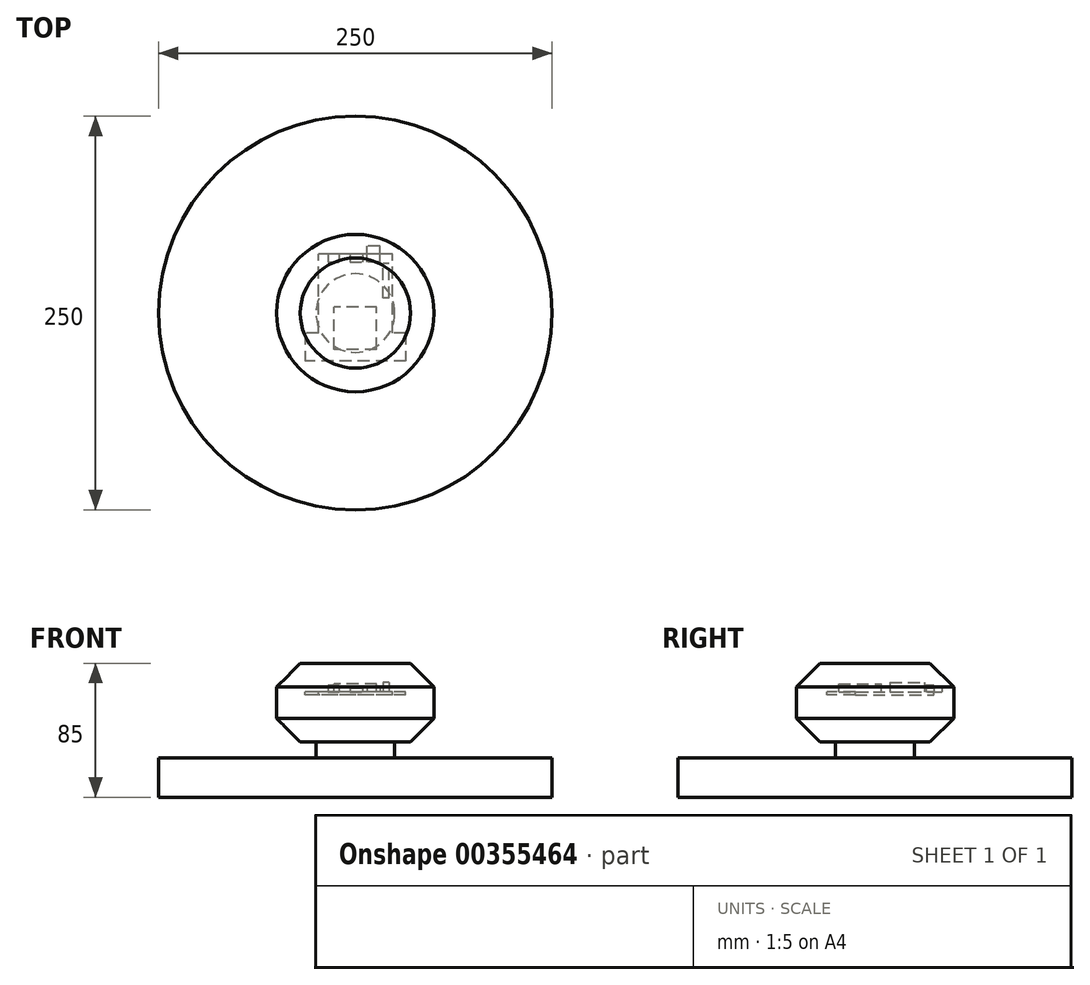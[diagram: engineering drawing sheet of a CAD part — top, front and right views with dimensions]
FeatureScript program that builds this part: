
annotation { "Feature Type Name" : "Feature", "Feature Type Description" : "" }
export const myFeature = defineFeature(function(context is Context, id is Id, definition is map)
    precondition{}
    {
        {
            var Q0;
            Q0=qCreatedBy(makeId("Top.planeOp"),FACE);
            var sketch = newSketch(context, id + "F0", { "sketchPlane" : qUnion([Q0])});
            skLineSegment(sketch, "E0.bottom", {"start": v(13.5, -13.5) * mm, "end": v(-13.5, -13.5) * mm});
            skLineSegment(sketch, "E0.top", {"start": v(13.5, 13.5) * mm, "end": v(-13.5, 13.5) * mm});
            skLineSegment(sketch, "E0.left", {"start": v(13.5, -13.5) * mm, "end": v(13.5, 13.5) * mm});
            skLineSegment(sketch, "E0.right", {"start": v(-13.5, -13.5) * mm, "end": v(-13.5, 13.5) * mm});
            skPoint(sketch, "E0.middle", {"position": v(0, 0) * mm});
            skSolve(sketch);
        }
        {
            var Q0;
            Q0=makeQuery(id+"F0.imprint","IMPRINT",FACE,{"disambiguationData":[TD([[makeQuery(id+"F0.imprint","IMPRINT",EDGE,{"derivedFrom":sQuery(id+"F0.wireOp",EDGE,"E0.bottom")}),-1.0]])]});
            extrude(context, id + "F1", {"entities" : qUnion([Q0]), "oppositeDirection" : true, "depth" : 2 * mm});
        }
        {
            var Q0;
            Q0=makeQuery(id+"F1.opExtrude","CAP_FACE",FACE,{"disambiguationData":[OSD([sQuery(id+"F0.wireOp",EDGE,"E0.bottom"),sQuery(id+"F0.wireOp",EDGE,"E0.top"),sQuery(id+"F0.wireOp",EDGE,"E0.left"),sQuery(id+"F0.wireOp",EDGE,"E0.right")])],"isStart":false});
            cPlane(context, id + "F2", {"entities" : qUnion([Q0]), "cplaneType" : CPlaneType.OFFSET, "offset" : 3 * mm, "width" : 150 * mm, "height" : 150 * mm});
        }
        {
            var Q0;
            Q0=qCreatedBy(id+"F2.planeOp",FACE);
            var sketch = newSketch(context, id + "F3", { "sketchPlane" : qUnion([Q0])});
            skLineSegment(sketch, "E1", {"start": v(0, 0) * mm, "end": v(0, -22) * mm, "construction": true});
            skLineSegment(sketch, "E2.bottom", {"start": v(23.5, 3) * mm, "end": v(-23.5, 3) * mm});
            skLineSegment(sketch, "E2.top", {"start": v(23.5, -47) * mm, "end": v(-23.5, -47) * mm});
            skLineSegment(sketch, "E2.left", {"start": v(23.5, 3) * mm, "end": v(23.5, -47) * mm});
            skLineSegment(sketch, "E2.right", {"start": v(-23.5, 3) * mm, "end": v(-23.5, -47) * mm});
            skPoint(sketch, "E2.middle", {"position": v(0, -22) * mm});
            skSolve(sketch);
        }
        {
            var Q0;
            Q0=makeQuery(id+"F3.imprint","IMPRINT",FACE,{"disambiguationData":[TD([[makeQuery(id+"F3.imprint","IMPRINT",EDGE,{"derivedFrom":sQuery(id+"F3.wireOp",EDGE,"E2.bottom")}),1.0]])]});
            extrude(context, id + "F4", {"entities" : qUnion([Q0]), "depth" : 2 * mm});
        }
        {
            var Q0;
            Q0=makeQuery(id+"F4.opExtrude","CAP_FACE",FACE,{"disambiguationData":[OSD([sQuery(id+"F3.wireOp",EDGE,"E2.bottom"),sQuery(id+"F3.wireOp",EDGE,"E2.top"),sQuery(id+"F3.wireOp",EDGE,"E2.left"),sQuery(id+"F3.wireOp",EDGE,"E2.right")])],"isStart":true});
            var sketch = newSketch(context, id + "F5", { "sketchPlane" : qUnion([Q0])});
            skLineSegment(sketch, "E3", {"start": v(0, -3) * mm, "end": v(0, -12) * mm, "construction": true});
            skPoint(sketch, "E3.endSnap0", {"position": v(0, -3) * mm});
            skLineSegment(sketch, "E4.bottom", {"start": v(32, -3) * mm, "end": v(-32, -3) * mm});
            skLineSegment(sketch, "E4.top", {"start": v(32, -21) * mm, "end": v(-32, -21) * mm});
            skLineSegment(sketch, "E4.left", {"start": v(32, -3) * mm, "end": v(32, -21) * mm});
            skLineSegment(sketch, "E4.right", {"start": v(-32, -3) * mm, "end": v(-32, -21) * mm});
            skPoint(sketch, "E4.middle", {"position": v(0, -12) * mm});
            skSolve(sketch);
        }
        {
            var Q0;
            Q0=makeQuery(id+"F5.imprint","IMPRINT",FACE,{"disambiguationData":[TD([[makeQuery(id+"F5.imprint","IMPRINT",EDGE,{"derivedFrom":sQuery(id+"F5.wireOp",EDGE,"E4.top")}),-1.0]])]});
            extrude(context, id + "F6", {"entities" : qUnion([Q0]), "operationType" : NewBodyOperationType.ADD, "oppositeDirection" : true, "depth" : 2 * mm});
        }
        {
            var Q0;
            Q0=makeQuery(id+"F1.opExtrude","CAP_FACE",FACE,{"disambiguationData":[OSD([sQuery(id+"F0.wireOp",EDGE,"E0.bottom"),sQuery(id+"F0.wireOp",EDGE,"E0.top"),sQuery(id+"F0.wireOp",EDGE,"E0.left"),sQuery(id+"F0.wireOp",EDGE,"E0.right")])],"isStart":false});
            var Q1;
            Q1=makeQuery(id+"F6.boolean.opBoolean","MERGE",FACE,{"derivedFrom":[makeQuery(id+"F4.opExtrude","CAP_FACE",FACE,{"disambiguationData":[OSD([sQuery(id+"F3.wireOp",EDGE,"E2.bottom"),sQuery(id+"F3.wireOp",EDGE,"E2.top"),sQuery(id+"F3.wireOp",EDGE,"E2.left"),sQuery(id+"F3.wireOp",EDGE,"E2.right")])],"isStart":true}),makeQuery(id+"F6.opExtrude","CAP_FACE",FACE,{"disambiguationData":[OSD([sQuery(id+"F5.wireOp",EDGE,"E4.bottom"),sQuery(id+"F5.wireOp",EDGE,"E4.top"),sQuery(id+"F5.wireOp",EDGE,"E4.left"),sQuery(id+"F5.wireOp",EDGE,"E4.right")])],"isStart":true})]});
            extrude(context, id + "F7", {"entities" : qUnion([Q0]), "endBound" : BoundingType.UP_TO_SURFACE, "endBoundEntityFace" : qUnion([Q1]), "depth" : 25 * mm});
        }
        {
            var Q0;
            Q0=makeQuery(id+"F6.boolean.opBoolean","MERGE",FACE,{"derivedFrom":[makeQuery(id+"F4.opExtrude","CAP_FACE",FACE,{"disambiguationData":[OSD([sQuery(id+"F3.wireOp",EDGE,"E2.bottom"),sQuery(id+"F3.wireOp",EDGE,"E2.top"),sQuery(id+"F3.wireOp",EDGE,"E2.left"),sQuery(id+"F3.wireOp",EDGE,"E2.right")])],"isStart":true}),makeQuery(id+"F6.opExtrude","CAP_FACE",FACE,{"disambiguationData":[OSD([sQuery(id+"F5.wireOp",EDGE,"E4.bottom"),sQuery(id+"F5.wireOp",EDGE,"E4.top"),sQuery(id+"F5.wireOp",EDGE,"E4.left"),sQuery(id+"F5.wireOp",EDGE,"E4.right")])],"isStart":true})]});
            var sketch = newSketch(context, id + "F8", { "sketchPlane" : qUnion([Q0])});
            skLineSegment(sketch, "E5", {"start": v(-23.5, 47) * mm, "end": v(-3.5, 47) * mm, "construction": true});
            skLineSegment(sketch, "E6.bottom", {"start": v(-3.5, 47) * mm, "end": v(4.5, 47) * mm});
            skLineSegment(sketch, "E6.top", {"start": v(-3.5, 42) * mm, "end": v(4.5, 42) * mm});
            skLineSegment(sketch, "E6.left", {"start": v(-3.5, 47) * mm, "end": v(-3.5, 42) * mm});
            skLineSegment(sketch, "E6.right", {"start": v(4.5, 47) * mm, "end": v(4.5, 42) * mm});
            skSolve(sketch);
        }
        {
            var Q0;
            Q0=makeQuery(id+"F8.imprint","IMPRINT",FACE,{"disambiguationData":[TD([[makeQuery(id+"F8.imprint","IMPRINT",EDGE,{"derivedFrom":sQuery(id+"F8.wireOp",EDGE,"E6.bottom")}),1.0]])]});
            extrude(context, id + "F9", {"entities" : qUnion([Q0]), "operationType" : NewBodyOperationType.ADD, "depth" : 2 * mm});
        }
        {
            var Q0;
            Q0=makeQuery(id+"F6.boolean.opBoolean","MERGE",FACE,{"derivedFrom":[makeQuery(id+"F4.opExtrude","CAP_FACE",FACE,{"disambiguationData":[OSD([sQuery(id+"F3.wireOp",EDGE,"E2.bottom"),sQuery(id+"F3.wireOp",EDGE,"E2.top"),sQuery(id+"F3.wireOp",EDGE,"E2.left"),sQuery(id+"F3.wireOp",EDGE,"E2.right")])],"isStart":true}),makeQuery(id+"F6.opExtrude","CAP_FACE",FACE,{"disambiguationData":[OSD([sQuery(id+"F5.wireOp",EDGE,"E4.bottom"),sQuery(id+"F5.wireOp",EDGE,"E4.top"),sQuery(id+"F5.wireOp",EDGE,"E4.left"),sQuery(id+"F5.wireOp",EDGE,"E4.right")])],"isStart":true})]});
            var sketch = newSketch(context, id + "F10", { "sketchPlane" : qUnion([Q0])});
            skLineSegment(sketch, "E7", {"start": v(23.5, 47) * mm, "end": v(11.5, 47) * mm, "construction": true});
            skLineSegment(sketch, "E8.bottom", {"start": v(15.5, 42) * mm, "end": v(7.5, 42) * mm});
            skLineSegment(sketch, "E8.top", {"start": v(15.5, 52) * mm, "end": v(7.5, 52) * mm});
            skLineSegment(sketch, "E8.left", {"start": v(15.5, 42) * mm, "end": v(15.5, 52) * mm});
            skLineSegment(sketch, "E8.right", {"start": v(7.5, 42) * mm, "end": v(7.5, 52) * mm});
            skPoint(sketch, "E8.middle", {"position": v(11.5, 47) * mm});
            skSolve(sketch);
        }
        {
            var Q0;
            {var subQ0=sQuery(id+"F10.wireOp",EDGE,"E8.bottom");Q0=makeQuery(id+"F10.imprint","IMPRINT",FACE,{"disambiguationData":[TD([[makeQuery(id+"F10.imprint","IMPRINT",EDGE,{"derivedFrom":subQ0}),-1.0]])]});}
            var Q1;
            {var subQ0=sQuery(id+"F10.wireOp",EDGE,"E8.top");Q1=makeQuery(id+"F10.imprint","IMPRINT",FACE,{"disambiguationData":[TD([[makeQuery(id+"F10.imprint","IMPRINT",EDGE,{"derivedFrom":subQ0}),1.0]])]});}
            extrude(context, id + "F11", {"entities" : qUnion([Q0, Q1]), "operationType" : NewBodyOperationType.ADD, "depth" : 3 * mm});
        }
        {
            var Q0;
            Q0=makeQuery(id+"F6.boolean.opBoolean","MERGE",FACE,{"derivedFrom":[makeQuery(id+"F4.opExtrude","CAP_FACE",FACE,{"disambiguationData":[OSD([sQuery(id+"F3.wireOp",EDGE,"E2.bottom"),sQuery(id+"F3.wireOp",EDGE,"E2.top"),sQuery(id+"F3.wireOp",EDGE,"E2.left"),sQuery(id+"F3.wireOp",EDGE,"E2.right")])],"isStart":true}),makeQuery(id+"F6.opExtrude","CAP_FACE",FACE,{"disambiguationData":[OSD([sQuery(id+"F5.wireOp",EDGE,"E4.bottom"),sQuery(id+"F5.wireOp",EDGE,"E4.top"),sQuery(id+"F5.wireOp",EDGE,"E4.left"),sQuery(id+"F5.wireOp",EDGE,"E4.right")])],"isStart":true})]});
            var sketch = newSketch(context, id + "F12", { "sketchPlane" : qUnion([Q0])});
            skLineSegment(sketch, "E9", {"start": v(23.5, 47) * mm, "end": v(23.5, 30) * mm, "construction": true});
            skLineSegment(sketch, "E10", {"start": v(23.5, 30) * mm, "end": v(19.5, 30) * mm, "construction": true});
            skLineSegment(sketch, "E11.bottom", {"start": v(21.5, 19) * mm, "end": v(17.5, 19) * mm});
            skLineSegment(sketch, "E11.top", {"start": v(21.5, 41) * mm, "end": v(17.5, 41) * mm});
            skLineSegment(sketch, "E11.left", {"start": v(21.5, 19) * mm, "end": v(21.5, 41) * mm});
            skLineSegment(sketch, "E11.right", {"start": v(17.5, 19) * mm, "end": v(17.5, 41) * mm});
            skPoint(sketch, "E11.middle", {"position": v(19.5, 30) * mm});
            skSolve(sketch);
        }
        {
            var Q0;
            Q0=makeQuery(id+"F12.imprint","IMPRINT",FACE,{"disambiguationData":[TD([[makeQuery(id+"F12.imprint","IMPRINT",EDGE,{"derivedFrom":sQuery(id+"F12.wireOp",EDGE,"E11.bottom")}),-1.0]])]});
            extrude(context, id + "F13", {"entities" : qUnion([Q0]), "operationType" : NewBodyOperationType.ADD, "depth" : 6 * mm});
        }
        {
            var Q0;
            Q0=makeQuery(id+"F6.boolean.opBoolean","MERGE",FACE,{"derivedFrom":[makeQuery(id+"F4.opExtrude","CAP_FACE",FACE,{"disambiguationData":[OSD([sQuery(id+"F3.wireOp",EDGE,"E2.bottom"),sQuery(id+"F3.wireOp",EDGE,"E2.top"),sQuery(id+"F3.wireOp",EDGE,"E2.left"),sQuery(id+"F3.wireOp",EDGE,"E2.right")])],"isStart":true}),makeQuery(id+"F6.opExtrude","CAP_FACE",FACE,{"disambiguationData":[OSD([sQuery(id+"F5.wireOp",EDGE,"E4.bottom"),sQuery(id+"F5.wireOp",EDGE,"E4.top"),sQuery(id+"F5.wireOp",EDGE,"E4.left"),sQuery(id+"F5.wireOp",EDGE,"E4.right")])],"isStart":true})]});
            var sketch = newSketch(context, id + "F14", { "sketchPlane" : qUnion([Q0])});
            skLineSegment(sketch, "E12", {"start": v(-23.5, 47) * mm, "end": v(-17.5, 47) * mm, "construction": true});
            skLineSegment(sketch, "E13.bottom", {"start": v(-17.5, 47) * mm, "end": v(-10.5, 47) * mm});
            skLineSegment(sketch, "E13.top", {"start": v(-17.5, 42) * mm, "end": v(-10.5, 42) * mm});
            skLineSegment(sketch, "E13.left", {"start": v(-17.5, 47) * mm, "end": v(-17.5, 42) * mm});
            skLineSegment(sketch, "E13.right", {"start": v(-10.5, 47) * mm, "end": v(-10.5, 42) * mm});
            skSolve(sketch);
        }
        {
            var Q0;
            Q0=makeQuery(id+"F14.imprint","IMPRINT",FACE,{"disambiguationData":[TD([[makeQuery(id+"F14.imprint","IMPRINT",EDGE,{"derivedFrom":sQuery(id+"F14.wireOp",EDGE,"E13.bottom")}),1.0]])]});
            extrude(context, id + "F15", {"entities" : qUnion([Q0]), "operationType" : NewBodyOperationType.ADD, "depth" : 4 * mm});
        }
        {
            var Q0;
            Q0=makeQuery(id+"F6.boolean.opBoolean","MERGE",FACE,{"derivedFrom":[makeQuery(id+"F4.opExtrude","CAP_FACE",FACE,{"disambiguationData":[OSD([sQuery(id+"F3.wireOp",EDGE,"E2.bottom"),sQuery(id+"F3.wireOp",EDGE,"E2.top"),sQuery(id+"F3.wireOp",EDGE,"E2.left"),sQuery(id+"F3.wireOp",EDGE,"E2.right")])],"isStart":false}),makeQuery(id+"F6.opExtrude","CAP_FACE",FACE,{"disambiguationData":[OSD([sQuery(id+"F5.wireOp",EDGE,"E4.bottom"),sQuery(id+"F5.wireOp",EDGE,"E4.top"),sQuery(id+"F5.wireOp",EDGE,"E4.left"),sQuery(id+"F5.wireOp",EDGE,"E4.right")])],"isStart":false})]});
            var sketch = newSketch(context, id + "F16", { "sketchPlane" : qUnion([Q0])});
            skCircle(sketch, "E14", {"center": v(0, -9.53) * mm, "radius": 44.23 * mm, "construction": true});
            skPoint(sketch, "E14.first.point", {"position": v(-23.5, -47) * mm});
            skPoint(sketch, "E14.second.point", {"position": v(23.5, -47) * mm});
            skCircle(sketch, "E15", {"center": v(0, -9.53) * mm, "radius": 47.5 * mm});
            skCircle(sketch, "E16", {"center": v(0, -9.53) * mm, "radius": 50 * mm});
            skSolve(sketch);
        }
        {
            var Q0;
            Q0=makeQuery(id+"F16.imprint","IMPRINT",FACE,{"disambiguationData":[TD([[makeQuery(id+"F16.imprint","IMPRINT",EDGE,{"derivedFrom":sQuery(id+"F16.wireOp",EDGE,"E15")}),-1.0]])]});
            var Q1;
            Q1=makeQuery(id+"F16.imprint","IMPRINT",FACE,{"disambiguationData":[TD([[makeQuery(id+"F16.imprint","IMPRINT",EDGE,{"derivedFrom":sQuery(id+"F16.wireOp",EDGE,"E15")}),1.0]])]});
            var Q2;
            {var subQ3=sQuery(id+"F3.wireOp",EDGE,"E2.top");Q2=makeQuery(id+"F16.imprint","IMPRINT",FACE,{"disambiguationData":[TD([[makeQuery(id+"F16.imprint","IMPRINT",EDGE,{"derivedFrom":makeQuery(id+"F4.opExtrude","CAP_EDGE",EDGE,{"disambiguationData":[OSD([subQ3])],"isStart":false})}),-1.0]])]});}
            extrude(context, id + "F17", {"entities" : qUnion([Q0, Q1, Q2]), "depth" : 30 * mm, "hasSecondDirection" : true, "secondDirectionOppositeDirection" : true, "secondDirectionDepth" : 20 * mm});
        }
        {
            var Q0;
            Q0=makeQuery(id+"F17.opExtrude","CAP_EDGE",EDGE,{"disambiguationData":[OSD([sQuery(id+"F16.wireOp",EDGE,"E16")])],"isStart":true});
            var Q1;
            Q1=makeQuery(id+"F17.opExtrude","CAP_EDGE",EDGE,{"disambiguationData":[OSD([sQuery(id+"F16.wireOp",EDGE,"E16")])],"isStart":false});
            chamfer(context, id + "F18", {"entities" : qUnion([Q0, Q1]), "width" : 15 * mm, "tangentPropagation" : true});
        }
        {
            var Q0;
            Q0=makeQuery(id+"F17.opExtrude","CAP_FACE",FACE,{"disambiguationData":[OSD([sQuery(id+"F16.wireOp",EDGE,"E16")])],"isStart":false});
            var sketch = newSketch(context, id + "F19", { "sketchPlane" : qUnion([Q0])});
            skCircle(sketch, "E17", {"center": v(0, -9.53) * mm, "radius": 25 * mm});
            skSolve(sketch);
        }
        {
            var Q0;
            Q0=makeQuery(id+"F19.imprint","IMPRINT",FACE,{"disambiguationData":[TD([[makeQuery(id+"F19.imprint","IMPRINT",EDGE,{"derivedFrom":sQuery(id+"F19.wireOp",EDGE,"E17")}),1.0]])]});
            extrude(context, id + "F20", {"entities" : qUnion([Q0]), "depth" : 10 * mm});
        }
        {
            var Q0;
            Q0=makeQuery(id+"F20.opExtrude","CAP_FACE",FACE,{"disambiguationData":[OSD([sQuery(id+"F19.wireOp",EDGE,"E17")])],"isStart":false});
            var sketch = newSketch(context, id + "F21", { "sketchPlane" : qUnion([Q0])});
            skCircle(sketch, "E18", {"center": v(0, -9.53) * mm, "radius": 125 * mm});
            skSolve(sketch);
        }
        {
            var Q0;
            Q0=makeQuery(id+"F21.imprint","IMPRINT",FACE,{"disambiguationData":[TD([[makeQuery(id+"F21.imprint","IMPRINT",EDGE,{"derivedFrom":sQuery(id+"F21.wireOp",EDGE,"E18")}),1.0]])]});
            var Q1;
            Q1=makeQuery(id+"F21.imprint","IMPRINT",FACE,{"disambiguationData":[TD([[makeQuery(id+"F21.imprint","IMPRINT",EDGE,{"derivedFrom":makeQuery(id+"F20.opExtrude","CAP_EDGE",EDGE,{"disambiguationData":[OSD([sQuery(id+"F19.wireOp",EDGE,"E17")])],"isStart":false})}),1.0]])]});
            extrude(context, id + "F22", {"entities" : qUnion([Q0, Q1]), "operationType" : NewBodyOperationType.ADD, "depth" : 25 * mm});
        }
    });
